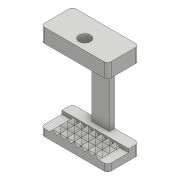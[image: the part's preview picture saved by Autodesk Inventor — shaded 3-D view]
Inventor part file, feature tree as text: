
AUTODESK INVENTOR PART (.ipt)
format: ipt  version: 2021 (Build 250183000, 183)  size: 252,928 bytes
history: native  units: mm
features: extrude x9, sketch x6, fillet x1
ambient origin geometry x8: Origin, YZ Plane, XZ Plane, XY Plane, X Axis, Y Axis, Z Axis, Center Point
bodies: Solid1 (feature_tree)
feature tree (16):
  extrude  "Extrusion1"  Depth=9.0mm
  sketch  "Sketch2"  dims[d2=3.0mm d3=0.0mm d4=3.0mm]
  extrude  "Extrusion2"  Depth=3.0mm
  extrude  "Extrusion8"  Depth=20.0mm TaperAngle=0.0deg
  extrude  "Extrusion9"  Depth=6.0mm
  fillet  "Fillet2"  [1 undecoded]
  extrude  "Extrusion12"  Depth=4.0mm TaperAngle=0.0deg
  extrude  "Extrusion13"  Depth=2.0mm
  extrude  "Extrusion14"  Depth=2.0mm
  extrude  "Extrusion15"  Depth=6.0mm TaperAngle=0.0deg
  extrude  "Extrusion16"  Depth=1.0mm
  sketch  "Sketch1"  dims[d0=19.0mm d1=9.0mm]
  sketch  "Sketch10"  dims[d5=1.5mm d6=20.0mm d7=0.0mm]
  sketch  "Sketch11"  dims[d23=1.0mm d24=6.0mm d25=135.0deg]
  sketch  "Sketch13"  dims[d26=90.0deg d27=4.0mm d28=0.0mm]
  sketch  "Sketch14"  dims[d30=135.0deg d31=40.0mm d33=2.0mm d34=10.0mm d36=10.0mm d38=40.0mm d40=2.0mm d41=10.0mm d43=10.0mm d45=6.0mm d46=0.0mm d47=1.0mm d65=4.0mm d66=0.0mm d67=3.0mm d68=3.3mm d69=10.0mm d70=0.0mm d71=10.0mm d72=0.0mm d73=0.75mm d74=5.0mm d75=10.0mm d76=0.0mm d77=10.0mm d78=0.0mm]
note: 1 required parameter value undecoded (feature->parameter linkage not recoverable at this tier; creation-order binding heuristic only, values carry confidence <= 0.55)
